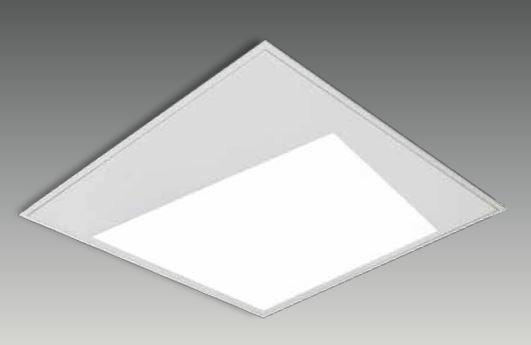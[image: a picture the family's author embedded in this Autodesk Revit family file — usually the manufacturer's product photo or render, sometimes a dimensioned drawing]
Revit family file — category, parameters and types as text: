
# Revit family: G 6060 SQU
name_source: partatom
category: Lighting Fixtures
revit_build: Autodesk Revit 2017 (Build: 20160225_1515(x64)
units: mm (PartAtom-declared; Revit-internal decimal feet)

## family parameters
Always vertical = Yes
Cut with Voids When Loaded = No
Host = Ceiling
Light Source = Yes
OmniClass Number = 23.80.70.11
OmniClass Title = Luminaries for Internal Lighting
Part Type = Normal
Room Calculation Point = No
Round Connector Dimension = Use Diameter
Shared = No

## types (4) — shared parameters
Color Filter = 16777215
Dimming Lamp Color Temperature Shift = <None>
Emit Shape Visible in Rendering = Yes
Emit from Rectangle Length = 570 mm  [stored 1.87008 ft]
Emit from Rectangle Width = 570 mm  [stored 1.87008 ft]
Light Source Symbol Size = 610 mm
Manufacturer = ARLIGHT
Type Image = G 6060 SQU.JPG

## per-type parameters (varying)
| type | Wattage Comments |
| GSQU.6060.28.30 | 28 |
| GSQU.6060.28.40 | 28 |
| GSQU.6060.36.30 | 36W |
| GSQU.6060.36.40 | 36W |

note: [stored X ft] marks values corroborated as IEEE doubles in the binary element streams (Revit-internal decimal feet)

## geometry (parser evidence)
native form markers: Sweep x2
no freeform markers — native parametric forms only
